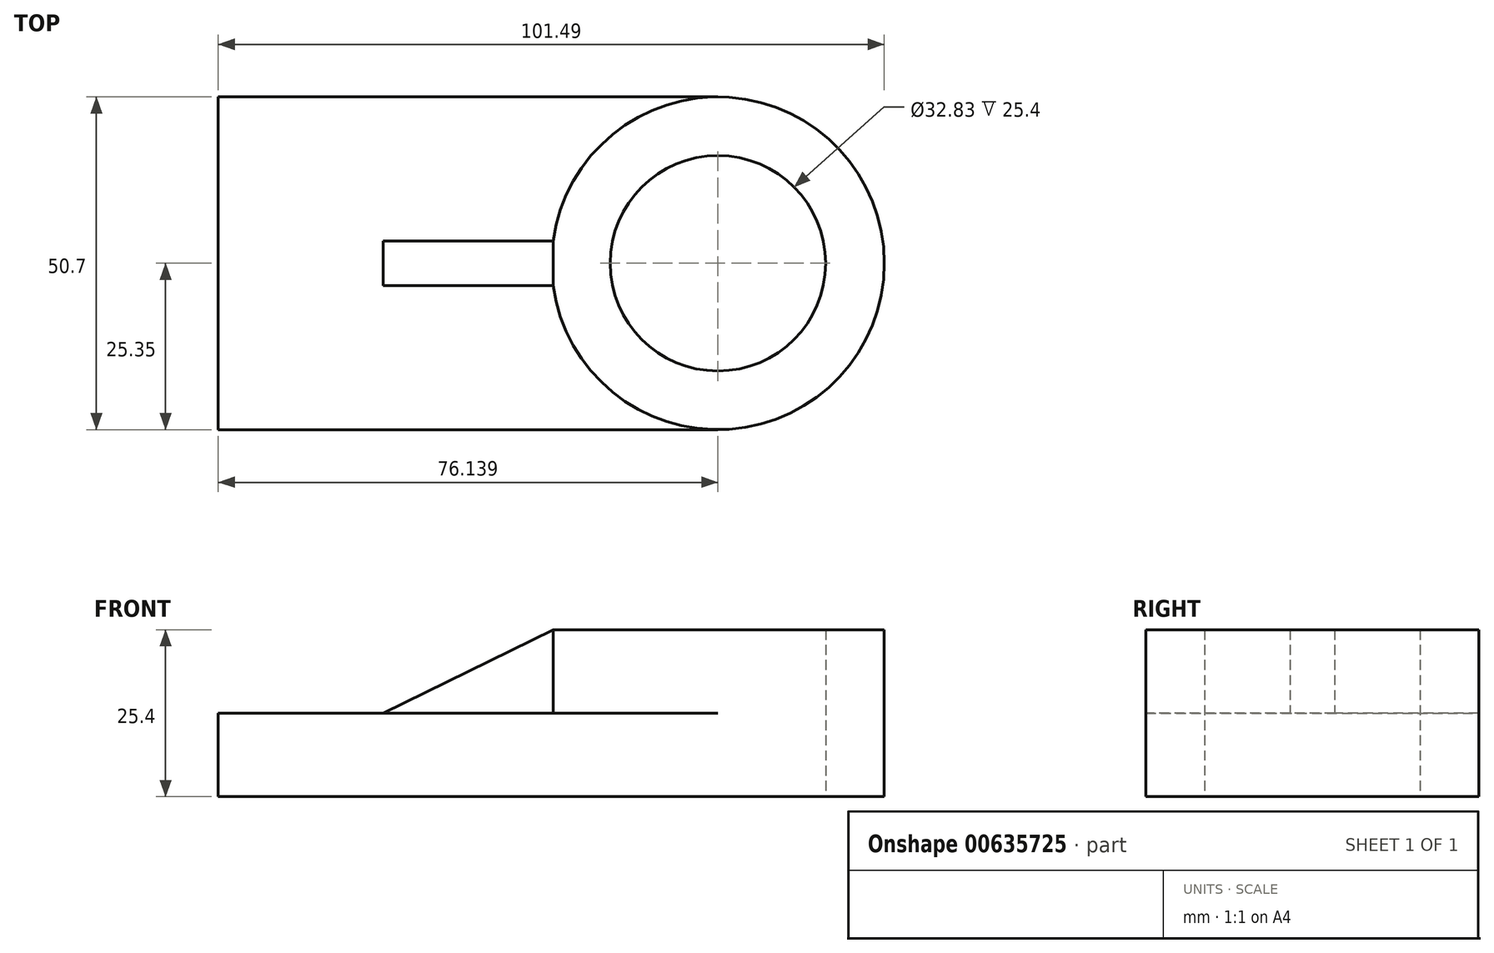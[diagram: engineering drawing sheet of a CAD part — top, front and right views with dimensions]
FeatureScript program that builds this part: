
annotation { "Feature Type Name" : "Feature", "Feature Type Description" : "" }
export const myFeature = defineFeature(function(context is Context, id is Id, definition is map)
    precondition{}
    {
        {
            var Q0;
            Q0=qCreatedBy(makeId("Top.planeOp"),FACE);
            var sketch = newSketch(context, id + "F0", { "sketchPlane" : qUnion([Q0])});
            skLineSegment(sketch, "E0.bottom", {"start": v(-38.07, -25.35) * mm, "end": v(38.07, -25.35) * mm});
            skLineSegment(sketch, "E0.top", {"start": v(-38.07, 25.35) * mm, "end": v(38.07, 25.35) * mm});
            skLineSegment(sketch, "E0.left", {"start": v(-38.07, -25.35) * mm, "end": v(-38.07, 25.35) * mm});
            skPoint(sketch, "E0.middle", {"position": v(0, 0) * mm});
            skCircle(sketch, "E1", {"center": v(38.07, 0) * mm, "radius": 25.35 * mm});
            skCircle(sketch, "E2", {"center": v(38.07, 0) * mm, "radius": 16.41 * mm});
            skSolve(sketch);
        }
        {
            var Q0;
            Q0=makeQuery(id+"F0.imprint","IMPRINT",FACE,{"disambiguationData":[TD([[makeQuery(id+"F0.imprint","IMPRINT",EDGE,{"derivedFrom":sQuery(id+"F0.wireOp",EDGE,"E2")}),-1.0]])]});
            extrude(context, id + "F1", {"entities" : qUnion([Q0]), "depth" : 25.4 * mm, "offsetDistance" : 25.4 * mm});
        }
        {
            var Q0;
            {var subQ0=sQuery(id+"F0.wireOp",EDGE,"E0.bottom");Q0=makeQuery(id+"F0.imprint","IMPRINT",FACE,{"disambiguationData":[TD([[makeQuery(id+"F0.imprint","IMPRINT",EDGE,{"derivedFrom":subQ0}),1.0]])]});}
            extrude(context, id + "F2", {"entities" : qUnion([Q0]), "operationType" : NewBodyOperationType.ADD, "depth" : 12.7 * mm, "offsetDistance" : 25.4 * mm});
        }
        {
            var Q0;
            Q0=makeQuery(id+"F2.opExtrude","CAP_FACE",FACE,{"disambiguationData":[OSD([sQuery(id+"F0.wireOp",EDGE,"E0.bottom"),sQuery(id+"F0.wireOp",EDGE,"E0.top"),sQuery(id+"F0.wireOp",EDGE,"E0.left"),sQuery(id+"F0.wireOp",EDGE,"E1")])],"isStart":false});
            var sketch = newSketch(context, id + "F3", { "sketchPlane" : qUnion([Q0])});
            skLineSegment(sketch, "E3.bottom", {"start": v(12.95, 3.4) * mm, "end": v(-12.95, 3.4) * mm});
            skLineSegment(sketch, "E3.top", {"start": v(12.95, -3.4) * mm, "end": v(-12.95, -3.4) * mm});
            skLineSegment(sketch, "E3.left", {"start": v(12.95, 3.4) * mm, "end": v(12.95, -3.4) * mm});
            skLineSegment(sketch, "E3.right", {"start": v(-12.95, 3.4) * mm, "end": v(-12.95, -3.4) * mm});
            skPoint(sketch, "E3.middle", {"position": v(0, 0) * mm});
            skSolve(sketch);
        }
        {
            var Q0;
            {var subQ0=sQuery(id+"F3.wireOp",EDGE,"E3.bottom");Q0=makeQuery(id+"F3.imprint","IMPRINT",FACE,{"disambiguationData":[TD([[makeQuery(id+"F3.imprint","IMPRINT",EDGE,{"derivedFrom":subQ0}),1.0]])]});}
            extrude(context, id + "F4", {"entities" : qUnion([Q0]), "operationType" : NewBodyOperationType.ADD, "depth" : 12.7 * mm, "offsetDistance" : 25.4 * mm});
        }
        {
            var Q0;
            Q0=makeQuery(id+"F4.opExtrude","SWEPT_FACE",FACE,{"disambiguationData":[OSD([sQuery(id+"F3.wireOp",EDGE,"E3.top")])]});
            var sketch = newSketch(context, id + "F5", { "sketchPlane" : qUnion([Q0])});
            skLineSegment(sketch, "E4", {"start": v(-12.95, 12.7) * mm, "end": v(12.95, 25.4) * mm});
            skSolve(sketch);
        }
        {
            var Q0;
            Q0=makeQuery(id+"F5.imprint","IMPRINT",FACE,{"disambiguationData":[TD([[makeQuery(id+"F5.imprint","IMPRINT",EDGE,{"derivedFrom":sQuery(id+"F5.wireOp",EDGE,"E4")}),1.0]])]});
            extrude(context, id + "F6", {"entities" : qUnion([Q0]), "operationType" : NewBodyOperationType.REMOVE, "oppositeDirection" : true, "depth" : 508 * mm, "offsetDistance" : 25.4 * mm});
        }
    });
